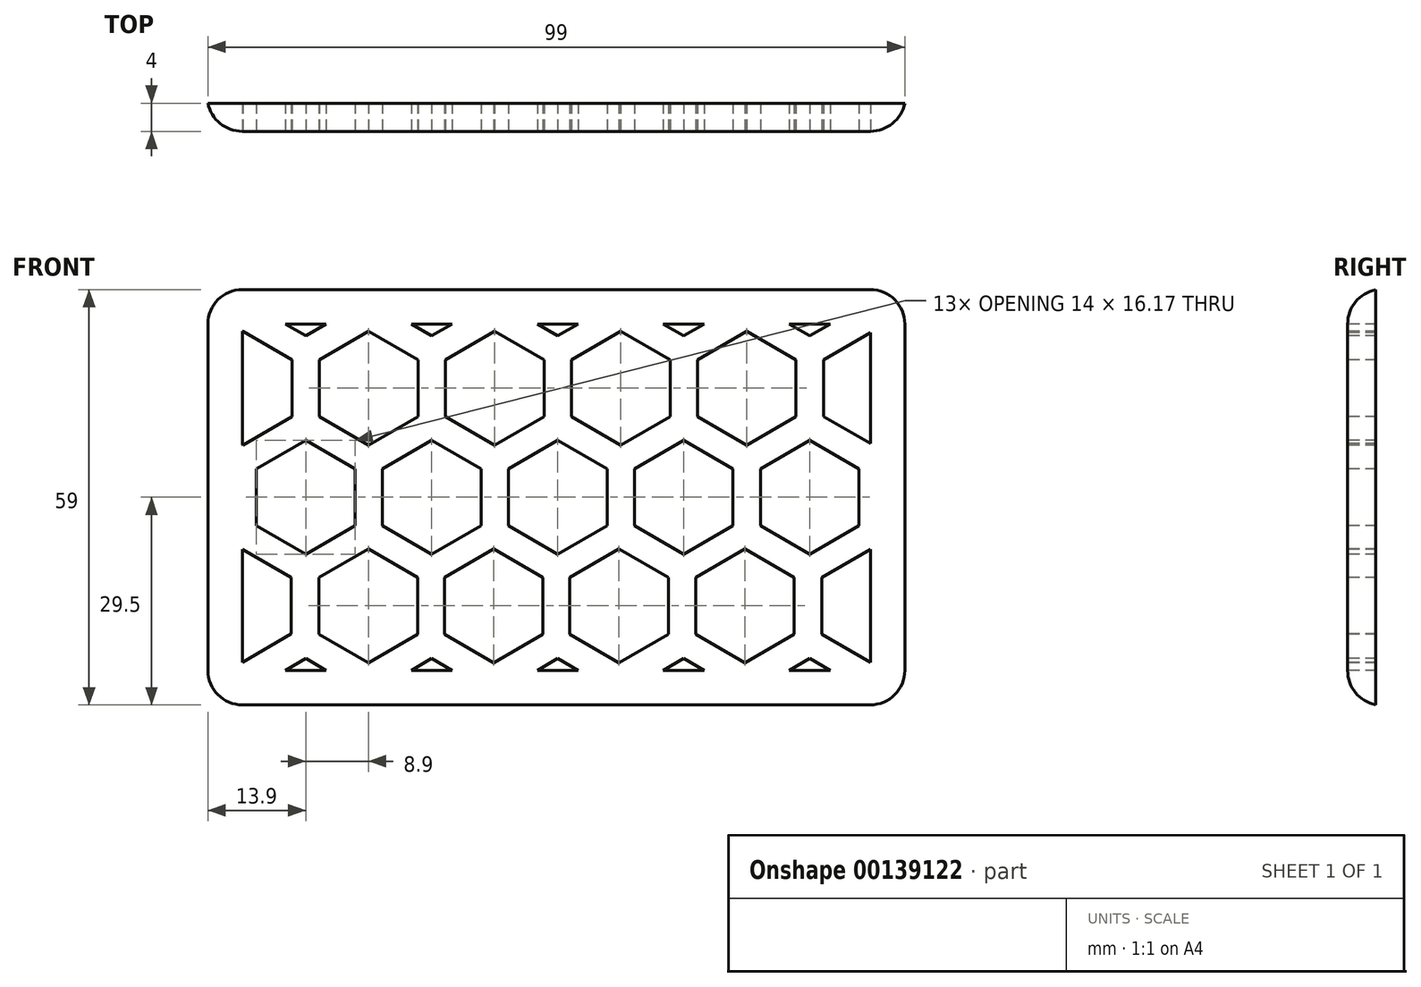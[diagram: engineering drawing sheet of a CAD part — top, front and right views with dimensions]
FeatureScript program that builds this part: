
annotation { "Feature Type Name" : "Feature", "Feature Type Description" : "" }
export const myFeature = defineFeature(function(context is Context, id is Id, definition is map)
    precondition{}
    {
        {
            var Q0;
            Q0=qCreatedBy(makeId("Front.planeOp"),FACE);
            var sketch = newSketch(context, id + "F0", { "sketchPlane" : qUnion([Q0])});
            skLineSegment(sketch, "E0.bottom", {"start": v(-49.5, -29.5) * mm, "end": v(49.5, -29.5) * mm});
            skLineSegment(sketch, "E0.top", {"start": v(-49.5, 29.5) * mm, "end": v(49.5, 29.5) * mm});
            skLineSegment(sketch, "E0.left", {"start": v(-49.5, -29.5) * mm, "end": v(-49.5, 29.5) * mm});
            skLineSegment(sketch, "E0.right", {"start": v(49.5, -29.5) * mm, "end": v(49.5, 29.5) * mm});
            skPoint(sketch, "E0.middle", {"position": v(0, 0) * mm});
            skSolve(sketch);
        }
        {
            var Q0;
            Q0=makeQuery(id+"F0.imprint","IMPRINT",FACE,{"disambiguationData":[TD([[makeQuery(id+"F0.imprint","IMPRINT",EDGE,{"derivedFrom":sQuery(id+"F0.wireOp",EDGE,"E0.bottom")}),1.0]])]});
            extrude(context, id + "F1", {"entities" : qUnion([Q0]), "depth" : 4 * mm});
        }
        {
            var Q0;
            Q0=makeQuery(id+"F1.opExtrude","CAP_EDGE",EDGE,{"disambiguationData":[OSD([sQuery(id+"F0.wireOp",EDGE,"E0.left")])],"isStart":false});
            var Q1;
            Q1=makeQuery(id+"F1.opExtrude","CAP_EDGE",EDGE,{"disambiguationData":[OSD([sQuery(id+"F0.wireOp",EDGE,"E0.top")])],"isStart":false});
            var Q2;
            Q2=makeQuery(id+"F1.opExtrude","CAP_EDGE",EDGE,{"disambiguationData":[OSD([sQuery(id+"F0.wireOp",EDGE,"E0.right")])],"isStart":false});
            var Q3;
            Q3=makeQuery(id+"F1.opExtrude","CAP_EDGE",EDGE,{"disambiguationData":[OSD([sQuery(id+"F0.wireOp",EDGE,"E0.bottom")])],"isStart":false});
            fillet(context, id + "F2", {"entities" : qUnion([Q0, Q1, Q2, Q3]), "radius" : 5 * mm, "tangentPropagation" : true, "allowEdgeOverflow" : false});
        }
        {
            var Q0;
            Q0=makeQuery(id+"F2.opFillet","BLEND_EDGE",EDGE,{"blendedFrom":[makeQuery(id+"F1.opExtrude","CAP_EDGE",EDGE,{"disambiguationData":[OSD([sQuery(id+"F0.wireOp",EDGE,"E0.top")])],"isStart":false}),makeQuery(id+"F1.opExtrude","CAP_EDGE",EDGE,{"disambiguationData":[OSD([sQuery(id+"F0.wireOp",EDGE,"E0.right")])],"isStart":false})],"blendedInto":[]});
            var Q1;
            Q1=makeQuery(id+"F2.opFillet","BLEND_EDGE",EDGE,{"blendedFrom":[makeQuery(id+"F1.opExtrude","CAP_EDGE",EDGE,{"disambiguationData":[OSD([sQuery(id+"F0.wireOp",EDGE,"E0.top")])],"isStart":false}),makeQuery(id+"F1.opExtrude","CAP_EDGE",EDGE,{"disambiguationData":[OSD([sQuery(id+"F0.wireOp",EDGE,"E0.left")])],"isStart":false})],"blendedInto":[]});
            var Q2;
            Q2=makeQuery(id+"F2.opFillet","BLEND_EDGE",EDGE,{"blendedFrom":[makeQuery(id+"F1.opExtrude","CAP_EDGE",EDGE,{"disambiguationData":[OSD([sQuery(id+"F0.wireOp",EDGE,"E0.bottom")])],"isStart":false}),makeQuery(id+"F1.opExtrude","CAP_EDGE",EDGE,{"disambiguationData":[OSD([sQuery(id+"F0.wireOp",EDGE,"E0.left")])],"isStart":false})],"blendedInto":[]});
            var Q3;
            Q3=makeQuery(id+"F2.opFillet","BLEND_EDGE",EDGE,{"blendedFrom":[makeQuery(id+"F1.opExtrude","CAP_EDGE",EDGE,{"disambiguationData":[OSD([sQuery(id+"F0.wireOp",EDGE,"E0.bottom")])],"isStart":false}),makeQuery(id+"F1.opExtrude","CAP_EDGE",EDGE,{"disambiguationData":[OSD([sQuery(id+"F0.wireOp",EDGE,"E0.right")])],"isStart":false})],"blendedInto":[]});
            fillet(context, id + "F3", {"entities" : qUnion([Q0, Q1, Q2, Q3]), "radius" : 5 * mm, "tangentPropagation" : true, "allowEdgeOverflow" : false});
        }
        {
            var Q0;
            Q0=makeQuery(id+"F1.opExtrude","CAP_FACE",FACE,{"disambiguationData":[OSD([sQuery(id+"F0.wireOp",EDGE,"E0.bottom"),sQuery(id+"F0.wireOp",EDGE,"E0.top"),sQuery(id+"F0.wireOp",EDGE,"E0.left"),sQuery(id+"F0.wireOp",EDGE,"E0.right")])],"isStart":false});
            var sketch = newSketch(context, id + "F4", { "sketchPlane" : qUnion([Q0])});
            skLineSegment(sketch, "E1", {"start": v(44.6, 0) * mm, "end": v(35.7, 0) * mm});
            skPoint(sketch, "E1.endSnap0", {"position": v(44.6, 0) * mm});
            skCircle(sketch, "E2.cCircle", {"center": v(35.7, 0) * mm, "radius": 8.9 * mm, "construction": true});
            skLineSegment(sketch, "E2.0", {"start": v(26.8, -5.14) * mm, "end": v(26.8, 5.14) * mm});
            skLineSegment(sketch, "E2.1", {"start": v(26.8, 5.14) * mm, "end": v(35.7, 10.28) * mm});
            skLineSegment(sketch, "E2.2", {"start": v(35.7, 10.28) * mm, "end": v(44.6, 5.14) * mm});
            skLineSegment(sketch, "E2.3", {"start": v(44.6, 5.14) * mm, "end": v(44.6, -5.14) * mm});
            skLineSegment(sketch, "E2.4", {"start": v(44.6, -5.14) * mm, "end": v(35.7, -10.28) * mm});
            skLineSegment(sketch, "E2.5", {"start": v(35.7, -10.28) * mm, "end": v(26.8, -5.14) * mm});
            skPoint(sketch, "E2.0.midPoint", {"position": v(26.8, 0) * mm});
            skLineSegment(sketch, "E3", {"start": v(26.8, 0) * mm, "end": v(17.9, 0) * mm});
            skCircle(sketch, "E4.cCircle", {"center": v(17.9, 0) * mm, "radius": 8.9 * mm, "construction": true});
            skLineSegment(sketch, "E4.0", {"start": v(9, -5.14) * mm, "end": v(9, 5.14) * mm});
            skLineSegment(sketch, "E4.1", {"start": v(9, 5.14) * mm, "end": v(17.9, 10.28) * mm});
            skLineSegment(sketch, "E4.2", {"start": v(17.9, 10.28) * mm, "end": v(26.8, 5.14) * mm});
            skLineSegment(sketch, "E4.3", {"start": v(26.8, 5.14) * mm, "end": v(26.8, -5.14) * mm});
            skLineSegment(sketch, "E4.4", {"start": v(26.8, -5.14) * mm, "end": v(17.9, -10.28) * mm});
            skLineSegment(sketch, "E4.5", {"start": v(17.9, -10.28) * mm, "end": v(9, -5.14) * mm});
            skPoint(sketch, "E4.0.midPoint", {"position": v(9, 0) * mm});
            skLineSegment(sketch, "E5", {"start": v(9, 0) * mm, "end": v(0.1, 0) * mm});
            skCircle(sketch, "E6.cCircle", {"center": v(0, 0) * mm, "radius": 8.9 * mm, "construction": true});
            skLineSegment(sketch, "E6.0", {"start": v(-8.9, -5.14) * mm, "end": v(-8.9, 5.14) * mm});
            skLineSegment(sketch, "E6.1", {"start": v(-8.9, 5.14) * mm, "end": v(0, 10.28) * mm});
            skLineSegment(sketch, "E6.2", {"start": v(0, 10.28) * mm, "end": v(8.9, 5.14) * mm});
            skLineSegment(sketch, "E6.3", {"start": v(8.9, 5.14) * mm, "end": v(8.9, -5.14) * mm});
            skLineSegment(sketch, "E6.4", {"start": v(8.9, -5.14) * mm, "end": v(0, -10.28) * mm});
            skLineSegment(sketch, "E6.5", {"start": v(0, -10.28) * mm, "end": v(-8.9, -5.14) * mm});
            skPoint(sketch, "E6.0.midPoint", {"position": v(-8.9, 0) * mm});
            skLineSegment(sketch, "E7", {"start": v(-8.9, 0) * mm, "end": v(-17.8, 0) * mm});
            skCircle(sketch, "E8.cCircle", {"center": v(-17.8, 0) * mm, "radius": 8.9 * mm, "construction": true});
            skLineSegment(sketch, "E8.0", {"start": v(-26.7, -5.14) * mm, "end": v(-26.7, 5.14) * mm});
            skLineSegment(sketch, "E8.1", {"start": v(-26.7, 5.14) * mm, "end": v(-17.8, 10.28) * mm});
            skLineSegment(sketch, "E8.2", {"start": v(-17.8, 10.28) * mm, "end": v(-8.9, 5.14) * mm});
            skLineSegment(sketch, "E8.3", {"start": v(-8.9, 5.14) * mm, "end": v(-8.9, -5.14) * mm});
            skLineSegment(sketch, "E8.4", {"start": v(-8.9, -5.14) * mm, "end": v(-17.8, -10.28) * mm});
            skLineSegment(sketch, "E8.5", {"start": v(-17.8, -10.28) * mm, "end": v(-26.7, -5.14) * mm});
            skPoint(sketch, "E8.0.midPoint", {"position": v(-26.7, 0) * mm});
            skLineSegment(sketch, "E9", {"start": v(-26.7, 0) * mm, "end": v(-35.6, 0) * mm});
            skCircle(sketch, "E10.cCircle", {"center": v(-35.6, 0) * mm, "radius": 9 * mm, "construction": true});
            skLineSegment(sketch, "E10.0", {"start": v(-44.6, -5.2) * mm, "end": v(-44.6, 5.2) * mm});
            skLineSegment(sketch, "E10.1", {"start": v(-44.6, 5.2) * mm, "end": v(-35.6, 10.4) * mm});
            skLineSegment(sketch, "E10.2", {"start": v(-35.6, 10.4) * mm, "end": v(-26.6, 5.2) * mm});
            skLineSegment(sketch, "E10.3", {"start": v(-26.6, 5.2) * mm, "end": v(-26.6, -5.2) * mm});
            skLineSegment(sketch, "E10.4", {"start": v(-26.6, -5.2) * mm, "end": v(-35.6, -10.4) * mm});
            skLineSegment(sketch, "E10.5", {"start": v(-35.6, -10.4) * mm, "end": v(-44.6, -5.2) * mm});
            skPoint(sketch, "E10.0.midPoint", {"position": v(-44.6, 0) * mm});
            skLineSegment(sketch, "E11", {"start": v(-31.1, 7.8) * mm, "end": v(-26.65, 15.5) * mm});
            skCircle(sketch, "E12.cCircle", {"center": v(-26.65, 15.5) * mm, "radius": 8.9 * mm, "construction": true});
            skLineSegment(sketch, "E12.0", {"start": v(-35.55, 10.36) * mm, "end": v(-35.55, 20.64) * mm});
            skLineSegment(sketch, "E12.1", {"start": v(-35.55, 20.64) * mm, "end": v(-28.7, 24.6) * mm});
            skLineSegment(sketch, "E12.2", {"start": v(-24.6, 24.6) * mm, "end": v(-17.75, 20.64) * mm});
            skLineSegment(sketch, "E12.3", {"start": v(-17.75, 20.64) * mm, "end": v(-17.75, 10.36) * mm});
            skLineSegment(sketch, "E12.4", {"start": v(-17.75, 10.36) * mm, "end": v(-26.65, 5.23) * mm});
            skLineSegment(sketch, "E12.5", {"start": v(-26.65, 5.23) * mm, "end": v(-35.55, 10.36) * mm});
            skPoint(sketch, "E12.0.midPoint", {"position": v(-35.55, 15.5) * mm});
            skLineSegment(sketch, "E13", {"start": v(-44.6, 24.6) * mm, "end": v(44.6, 24.6) * mm});
            skLineSegment(sketch, "E14", {"start": v(-44.6, 24.6) * mm, "end": v(-44.6, -24.6) * mm});
            skLineSegment(sketch, "E15", {"start": v(-44.6, -24.6) * mm, "end": v(44.6, -24.6) * mm});
            skLineSegment(sketch, "E16", {"start": v(44.6, -24.6) * mm, "end": v(44.6, 24.6) * mm});
            skPoint(sketch, "E17.orphan", {"position": v(-26.65, 25.78) * mm});
            skLineSegment(sketch, "E18", {"start": v(-40.1, 7.8) * mm, "end": v(-44.55, 15.5) * mm});
            skArc(sketch, "E19.cCircle", {"start": v(-44.6, 6.6) * mm, "mid": v(-35.65, 15.5) * mm, "end": v(-44.6, 24.4) * mm, "construction": true});
            skLineSegment(sketch, "E19.2", {"start": v(-44.55, 25.78) * mm, "end": v(-35.65, 20.64) * mm});
            skLineSegment(sketch, "E19.3", {"start": v(-35.65, 20.64) * mm, "end": v(-35.65, 10.36) * mm});
            skLineSegment(sketch, "E19.4", {"start": v(-35.65, 10.36) * mm, "end": v(-44.55, 5.23) * mm});
            skLineSegment(sketch, "E19.5", {"start": v(-44.55, 5.23) * mm, "end": v(-44.6, 5.26) * mm});
            skPoint(sketch, "E19.0.midPoint", {"position": v(-53.45, 15.5) * mm});
            skPoint(sketch, "E20.orphan", {"position": v(-53.45, 20.64) * mm});
            skPoint(sketch, "E21.orphan", {"position": v(-53.45, 10.36) * mm});
            skCircle(sketch, "E22.cCircle", {"center": v(-8.9, 15.42) * mm, "radius": 8.9 * mm, "construction": true});
            skLineSegment(sketch, "E22.0", {"start": v(-17.42, 9.66) * mm, "end": v(-18.14, 19.92) * mm});
            skLineSegment(sketch, "E22.1", {"start": v(-18.14, 19.92) * mm, "end": v(-11.2, 24.6) * mm});
            skLineSegment(sketch, "E22.2", {"start": v(-7.43, 24.6) * mm, "end": v(-0.38, 21.17) * mm});
            skLineSegment(sketch, "E22.3", {"start": v(-0.38, 21.17) * mm, "end": v(0.34, 10.91) * mm});
            skLineSegment(sketch, "E22.4", {"start": v(0.34, 10.91) * mm, "end": v(-8.18, 5.16) * mm});
            skLineSegment(sketch, "E22.5", {"start": v(-8.18, 5.16) * mm, "end": v(-17.42, 9.66) * mm});
            skPoint(sketch, "E22.0.midPoint", {"position": v(-17.78, 14.8) * mm});
            skPoint(sketch, "E23.orphan", {"position": v(-9.62, 25.67) * mm});
            skLineSegment(sketch, "E24", {"start": v(-22.25, -7.7) * mm, "end": v(-26.7, -15.42) * mm});
            skCircle(sketch, "E25.cCircle", {"center": v(-26.7, -15.42) * mm, "radius": 8.9 * mm, "construction": true});
            skLineSegment(sketch, "E25.0", {"start": v(-35.6, -20.55) * mm, "end": v(-35.6, -10.28) * mm});
            skLineSegment(sketch, "E25.1", {"start": v(-35.6, -10.28) * mm, "end": v(-26.7, -5.14) * mm});
            skLineSegment(sketch, "E25.2", {"start": v(-26.7, -5.14) * mm, "end": v(-17.8, -10.28) * mm});
            skLineSegment(sketch, "E25.3", {"start": v(-17.8, -10.28) * mm, "end": v(-17.8, -20.55) * mm});
            skLineSegment(sketch, "E25.4", {"start": v(-17.8, -20.55) * mm, "end": v(-24.81, -24.6) * mm});
            skLineSegment(sketch, "E25.5", {"start": v(-28.59, -24.6) * mm, "end": v(-35.6, -20.55) * mm});
            skPoint(sketch, "E25.0.midPoint", {"position": v(-35.6, -15.42) * mm});
            skLineSegment(sketch, "E26", {"start": v(-4.45, -7.7) * mm, "end": v(-8.9, -15.42) * mm});
            skPoint(sketch, "E26.endSnap0", {"position": v(-17.8, -15.42) * mm});
            skCircle(sketch, "E27.cCircle", {"center": v(-8.9, -15.42) * mm, "radius": 8.9 * mm, "construction": true});
            skLineSegment(sketch, "E27.0", {"start": v(-17.8, -20.55) * mm, "end": v(-17.8, -10.28) * mm});
            skLineSegment(sketch, "E27.1", {"start": v(-17.8, -10.28) * mm, "end": v(-8.9, -5.14) * mm});
            skLineSegment(sketch, "E27.2", {"start": v(-8.9, -5.14) * mm, "end": v(0, -10.28) * mm});
            skLineSegment(sketch, "E27.3", {"start": v(0, -10.28) * mm, "end": v(0, -20.55) * mm});
            skLineSegment(sketch, "E27.4", {"start": v(0, -20.55) * mm, "end": v(-7.01, -24.6) * mm});
            skLineSegment(sketch, "E27.5", {"start": v(-10.79, -24.6) * mm, "end": v(-17.8, -20.55) * mm});
            skLineSegment(sketch, "E28", {"start": v(4.45, -7.7) * mm, "end": v(8.9, -15.42) * mm});
            skCircle(sketch, "E29.cCircle", {"center": v(8.9, -15.42) * mm, "radius": 8.85 * mm, "construction": true});
            skPoint(sketch, "E29.cCircle.perimeterSnap0", {"position": v(0, -15.42) * mm});
            skLineSegment(sketch, "E29.0", {"start": v(0.05, -20.52) * mm, "end": v(0.05, -10.3) * mm});
            skLineSegment(sketch, "E29.1", {"start": v(0.05, -10.3) * mm, "end": v(8.9, -5.2) * mm});
            skLineSegment(sketch, "E29.2", {"start": v(8.9, -5.2) * mm, "end": v(17.75, -10.3) * mm});
            skLineSegment(sketch, "E29.3", {"start": v(17.75, -10.3) * mm, "end": v(17.75, -20.52) * mm});
            skLineSegment(sketch, "E29.4", {"start": v(17.75, -20.52) * mm, "end": v(10.69, -24.6) * mm});
            skLineSegment(sketch, "E29.5", {"start": v(7.11, -24.6) * mm, "end": v(0.05, -20.52) * mm});
            skPoint(sketch, "E29.0.midPoint", {"position": v(0.05, -15.42) * mm});
            skPoint(sketch, "E29.0.midPoint.positionSnap0", {"position": v(0, -15.42) * mm});
            skLineSegment(sketch, "E30", {"start": v(13.45, 7.7) * mm, "end": v(9, 15.42) * mm});
            skCircle(sketch, "E31.cCircle", {"center": v(9, 15.42) * mm, "radius": 8.9 * mm, "construction": true});
            skLineSegment(sketch, "E31.0", {"start": v(0.1, 10.28) * mm, "end": v(0.1, 20.55) * mm});
            skLineSegment(sketch, "E31.1", {"start": v(0.1, 20.55) * mm, "end": v(9, 25.7) * mm});
            skLineSegment(sketch, "E31.2", {"start": v(9, 25.7) * mm, "end": v(17.9, 20.55) * mm});
            skLineSegment(sketch, "E31.3", {"start": v(17.9, 20.55) * mm, "end": v(17.9, 10.28) * mm});
            skLineSegment(sketch, "E31.4", {"start": v(17.9, 10.28) * mm, "end": v(9, 5.14) * mm});
            skLineSegment(sketch, "E31.5", {"start": v(9, 5.14) * mm, "end": v(0.1, 10.28) * mm});
            skPoint(sketch, "E31.0.midPoint", {"position": v(0.1, 15.42) * mm});
            skLineSegment(sketch, "E32", {"start": v(22.35, 7.7) * mm, "end": v(26.8, 15.42) * mm});
            skCircle(sketch, "E33.cCircle", {"center": v(26.8, 15.42) * mm, "radius": 8.9 * mm, "construction": true});
            skLineSegment(sketch, "E33.0", {"start": v(17.9, 10.28) * mm, "end": v(17.9, 20.55) * mm});
            skLineSegment(sketch, "E33.1", {"start": v(17.9, 20.55) * mm, "end": v(24.91, 24.6) * mm});
            skLineSegment(sketch, "E33.2", {"start": v(26.8, 25.7) * mm, "end": v(26.83, 25.68) * mm});
            skLineSegment(sketch, "E33.3", {"start": v(35.7, 20.55) * mm, "end": v(35.7, 10.28) * mm});
            skLineSegment(sketch, "E33.4", {"start": v(35.7, 10.28) * mm, "end": v(26.8, 5.14) * mm});
            skLineSegment(sketch, "E33.5", {"start": v(26.8, 5.14) * mm, "end": v(17.9, 10.28) * mm});
            skPoint(sketch, "E33.0.midPoint", {"position": v(17.9, 15.42) * mm});
            skLineSegment(sketch, "E34", {"start": v(22.35, -7.7) * mm, "end": v(26.8, -15.42) * mm});
            skCircle(sketch, "E35.cCircle", {"center": v(26.8, -15.42) * mm, "radius": 8.9 * mm, "construction": true});
            skLineSegment(sketch, "E35.0", {"start": v(17.9, -20.55) * mm, "end": v(17.9, -10.28) * mm});
            skLineSegment(sketch, "E35.1", {"start": v(17.9, -10.28) * mm, "end": v(26.8, -5.14) * mm});
            skLineSegment(sketch, "E35.2", {"start": v(26.8, -5.14) * mm, "end": v(35.7, -10.28) * mm});
            skLineSegment(sketch, "E35.3", {"start": v(35.7, -10.28) * mm, "end": v(35.7, -20.55) * mm});
            skLineSegment(sketch, "E35.4", {"start": v(35.7, -20.55) * mm, "end": v(28.7, -24.6) * mm});
            skLineSegment(sketch, "E35.5", {"start": v(24.91, -24.6) * mm, "end": v(17.9, -20.55) * mm});
            skPoint(sketch, "E35.0.midPoint", {"position": v(17.9, -15.42) * mm});
            skLineSegment(sketch, "E36", {"start": v(35.7, -15.42) * mm, "end": v(44.6, -15.42) * mm});
            skArc(sketch, "E37.cCircle", {"start": v(44.6, -6.52) * mm, "mid": v(35.7, -15.42) * mm, "end": v(44.6, -24.32) * mm, "construction": true});
            skLineSegment(sketch, "E37.0", {"start": v(35.7, -20.55) * mm, "end": v(35.7, -10.28) * mm});
            skLineSegment(sketch, "E37.1", {"start": v(35.7, -10.28) * mm, "end": v(44.6, -5.14) * mm});
            skLineSegment(sketch, "E37.5", {"start": v(44.6, -25.7) * mm, "end": v(35.7, -20.55) * mm});
            skPoint(sketch, "E37.0.midPoint", {"position": v(35.7, -15.42) * mm});
            skLineSegment(sketch, "E38", {"start": v(35.7, 15.42) * mm, "end": v(44.6, 15.42) * mm});
            skArc(sketch, "E39.cCircle", {"start": v(44.6, 24.27) * mm, "mid": v(35.75, 15.42) * mm, "end": v(44.6, 6.57) * mm, "construction": true});
            skLineSegment(sketch, "E39.0", {"start": v(35.75, 10.3) * mm, "end": v(35.75, 20.52) * mm});
            skLineSegment(sketch, "E39.1", {"start": v(35.75, 20.52) * mm, "end": v(42.81, 24.6) * mm});
            skLineSegment(sketch, "E39.5", {"start": v(44.6, 5.2) * mm, "end": v(35.75, 10.3) * mm});
            skPoint(sketch, "E39.0.midPoint", {"position": v(35.75, 15.42) * mm});
            skLineSegment(sketch, "E40", {"start": v(40.18, 23.08) * mm, "end": v(35.73, 30.79) * mm});
            skArc(sketch, "E41.cCircle", {"start": v(29.33, 24.6) * mm, "mid": v(35.73, 21.89) * mm, "end": v(42.12, 24.6) * mm, "construction": true});
            skLineSegment(sketch, "E41.0", {"start": v(26.83, 25.65) * mm, "end": v(26.83, 25.68) * mm});
            skLineSegment(sketch, "E41.4", {"start": v(44.63, 25.65) * mm, "end": v(35.73, 20.51) * mm});
            skLineSegment(sketch, "E41.5", {"start": v(35.73, 20.51) * mm, "end": v(28.64, 24.6) * mm});
            skPoint(sketch, "E41.0.midPoint", {"position": v(26.83, 30.79) * mm});
            skLineSegment(sketch, "E42", {"start": v(22.35, 23.12) * mm, "end": v(17.9, 30.83) * mm});
            skArc(sketch, "E43.cCircle", {"start": v(11.54, 24.6) * mm, "mid": v(17.9, 21.93) * mm, "end": v(24.26, 24.6) * mm, "construction": true});
            skLineSegment(sketch, "E43.0", {"start": v(9, 25.7) * mm, "end": v(9, 35.97) * mm});
            skLineSegment(sketch, "E43.4", {"start": v(24.91, 24.6) * mm, "end": v(17.9, 20.55) * mm});
            skLineSegment(sketch, "E43.5", {"start": v(17.9, 20.55) * mm, "end": v(10.9, 24.6) * mm});
            skPoint(sketch, "E43.0.midPoint", {"position": v(9, 30.83) * mm});
            skLineSegment(sketch, "E44", {"start": v(9, 30.83) * mm, "end": v(0.1, 30.83) * mm});
            skArc(sketch, "E45.cCircle", {"start": v(-6.26, 24.6) * mm, "mid": v(8.34, 34.2) * mm, "end": v(-8.8, 30.83) * mm, "construction": true});
            skLineSegment(sketch, "E45.1", {"start": v(-8.8, 35.97) * mm, "end": v(0.1, 41.1) * mm});
            skLineSegment(sketch, "E45.2", {"start": v(0.1, 41.1) * mm, "end": v(9, 35.97) * mm});
            skLineSegment(sketch, "E45.3", {"start": v(9, 30.83) * mm, "end": v(9, 25.7) * mm});
            skLineSegment(sketch, "E45.4", {"start": v(9, 25.7) * mm, "end": v(0.1, 20.55) * mm});
            skLineSegment(sketch, "E45.5", {"start": v(0.1, 20.55) * mm, "end": v(-6.9, 24.6) * mm});
            skPoint(sketch, "E45.0.midPoint", {"position": v(-8.8, 30.83) * mm});
            skPoint(sketch, "E46.orphan", {"position": v(-26.7, -25.7) * mm});
            skPoint(sketch, "E47.orphan", {"position": v(-8.9, -25.7) * mm});
            skPoint(sketch, "E48.orphan", {"position": v(8.9, -25.63) * mm});
            skLineSegment(sketch, "E49.0.1", {"start": v(-44.6, -24.6) * mm, "end": v(-44.6, -29.5) * mm});
            skLineSegment(sketch, "E49.0.2", {"start": v(-44.6, -29.5) * mm, "end": v(44.6, -29.5) * mm});
            skLineSegment(sketch, "E49.0.3", {"start": v(44.6, -29.5) * mm, "end": v(44.6, -24.6) * mm});
            skPoint(sketch, "E50.orphan", {"position": v(44.6, 25.63) * mm});
            skLineSegment(sketch, "E51.trimOffspring", {"start": v(28.7, 24.6) * mm, "end": v(35.7, 20.55) * mm});
            skPoint(sketch, "E52.trimOffspring.end.orphan", {"position": v(26.83, 35.93) * mm});
            skPoint(sketch, "E53.orphan", {"position": v(-8.8, 25.7) * mm});
            skCircle(sketch, "E54.cCircle", {"center": v(-35.6, 0) * mm, "radius": 7 * mm, "construction": true});
            skLineSegment(sketch, "E54.0", {"start": v(-42.6, -4.04) * mm, "end": v(-42.6, 4.04) * mm});
            skLineSegment(sketch, "E54.1", {"start": v(-42.6, 4.04) * mm, "end": v(-35.6, 8.08) * mm});
            skLineSegment(sketch, "E54.2", {"start": v(-35.6, 8.08) * mm, "end": v(-28.6, 4.04) * mm});
            skLineSegment(sketch, "E54.3", {"start": v(-28.6, 4.04) * mm, "end": v(-28.6, -4.04) * mm});
            skLineSegment(sketch, "E54.4", {"start": v(-28.6, -4.04) * mm, "end": v(-35.6, -8.08) * mm});
            skLineSegment(sketch, "E54.5", {"start": v(-35.6, -8.08) * mm, "end": v(-42.6, -4.04) * mm});
            skPoint(sketch, "E54.0.midPoint", {"position": v(-42.6, 0) * mm});
            skCircle(sketch, "E55.cCircle", {"center": v(-26.65, 15.5) * mm, "radius": 7 * mm, "construction": true});
            skLineSegment(sketch, "E55.0", {"start": v(-33.65, 11.46) * mm, "end": v(-33.65, 19.54) * mm});
            skLineSegment(sketch, "E55.1", {"start": v(-33.65, 19.54) * mm, "end": v(-26.65, 23.59) * mm});
            skLineSegment(sketch, "E55.2", {"start": v(-26.65, 23.59) * mm, "end": v(-19.65, 19.54) * mm});
            skLineSegment(sketch, "E55.3", {"start": v(-19.65, 19.54) * mm, "end": v(-19.65, 11.46) * mm});
            skLineSegment(sketch, "E55.4", {"start": v(-19.65, 11.46) * mm, "end": v(-26.65, 7.42) * mm});
            skLineSegment(sketch, "E55.5", {"start": v(-26.65, 7.42) * mm, "end": v(-33.65, 11.46) * mm});
            skPoint(sketch, "E55.0.midPoint", {"position": v(-33.65, 15.5) * mm});
            skCircle(sketch, "E56.cCircle", {"center": v(-26.7, -15.42) * mm, "radius": 7 * mm, "construction": true});
            skLineSegment(sketch, "E56.0", {"start": v(-33.7, -19.46) * mm, "end": v(-33.7, -11.37) * mm});
            skLineSegment(sketch, "E56.1", {"start": v(-33.7, -11.37) * mm, "end": v(-26.7, -7.33) * mm});
            skLineSegment(sketch, "E56.2", {"start": v(-26.7, -7.33) * mm, "end": v(-19.7, -11.37) * mm});
            skLineSegment(sketch, "E56.3", {"start": v(-19.7, -11.37) * mm, "end": v(-19.7, -19.46) * mm});
            skLineSegment(sketch, "E56.4", {"start": v(-19.7, -19.46) * mm, "end": v(-26.7, -23.5) * mm});
            skLineSegment(sketch, "E56.5", {"start": v(-26.7, -23.5) * mm, "end": v(-33.7, -19.46) * mm});
            skPoint(sketch, "E56.0.midPoint", {"position": v(-33.7, -15.42) * mm});
            skCircle(sketch, "E57.cCircle", {"center": v(-8.9, -15.42) * mm, "radius": 7 * mm, "construction": true});
            skLineSegment(sketch, "E57.0", {"start": v(-15.9, -19.46) * mm, "end": v(-15.9, -11.37) * mm});
            skLineSegment(sketch, "E57.1", {"start": v(-15.9, -11.37) * mm, "end": v(-8.9, -7.33) * mm});
            skLineSegment(sketch, "E57.2", {"start": v(-8.9, -7.33) * mm, "end": v(-1.9, -11.37) * mm});
            skLineSegment(sketch, "E57.3", {"start": v(-1.9, -11.37) * mm, "end": v(-1.9, -19.46) * mm});
            skLineSegment(sketch, "E57.4", {"start": v(-1.9, -19.46) * mm, "end": v(-8.9, -23.5) * mm});
            skLineSegment(sketch, "E57.5", {"start": v(-8.9, -23.5) * mm, "end": v(-15.9, -19.46) * mm});
            skPoint(sketch, "E57.0.midPoint", {"position": v(-15.9, -15.42) * mm});
            skPoint(sketch, "E58.cCircle.perimeterSnap0", {"position": v(4.55, 7.7) * mm});
            skPoint(sketch, "E58.0.midPoint.positionSnap0", {"position": v(4.55, 7.7) * mm});
            skCircle(sketch, "E59.cCircle", {"center": v(8.9, -15.42) * mm, "radius": 7 * mm, "construction": true});
            skLineSegment(sketch, "E59.0", {"start": v(1.9, -19.46) * mm, "end": v(1.9, -11.37) * mm});
            skLineSegment(sketch, "E59.1", {"start": v(1.9, -11.37) * mm, "end": v(8.9, -7.33) * mm});
            skLineSegment(sketch, "E59.2", {"start": v(8.9, -7.33) * mm, "end": v(15.9, -11.37) * mm});
            skLineSegment(sketch, "E59.3", {"start": v(15.9, -11.37) * mm, "end": v(15.9, -19.46) * mm});
            skLineSegment(sketch, "E59.4", {"start": v(15.9, -19.46) * mm, "end": v(8.9, -23.5) * mm});
            skLineSegment(sketch, "E59.5", {"start": v(8.9, -23.5) * mm, "end": v(1.9, -19.46) * mm});
            skPoint(sketch, "E59.0.midPoint", {"position": v(1.9, -15.42) * mm});
            skSolve(sketch);
        }
        {
            var Q0;
            {var subQ3=sQuery(id+"F4.wireOp",EDGE,"E59.0");Q0=makeQuery(id+"F4.imprint","IMPRINT",FACE,{"disambiguationData":[TD([[makeQuery(id+"F4.imprint","IMPRINT",EDGE,{"derivedFrom":subQ3}),-1.0]])]});}
            var Q1;
            Q1=makeQuery(id+"F4.imprint","IMPRINT",FACE,{"disambiguationData":[TD([[makeQuery(id+"F4.imprint","IMPRINT",EDGE,{"derivedFrom":sQuery(id+"F4.wireOp",EDGE,"E57.0")}),-1.0]])]});
            var Q2;
            Q2=makeQuery(id+"F4.imprint","IMPRINT",FACE,{"disambiguationData":[TD([[makeQuery(id+"F4.imprint","IMPRINT",EDGE,{"derivedFrom":sQuery(id+"F4.wireOp",EDGE,"E56.0")}),-1.0]])]});
            var Q3;
            Q3=makeQuery(id+"F4.imprint","IMPRINT",FACE,{"disambiguationData":[TD([[makeQuery(id+"F4.imprint","IMPRINT",EDGE,{"derivedFrom":sQuery(id+"F4.wireOp",EDGE,"E54.0")}),-1.0]])]});
            var Q4;
            {var subQ0=sQuery(id+"F4.wireOp",EDGE,"E55.0");Q4=makeQuery(id+"F4.imprint","IMPRINT",FACE,{"disambiguationData":[TD([[makeQuery(id+"F4.imprint","IMPRINT",EDGE,{"derivedFrom":subQ0}),-1.0]])]});}
            extrude(context, id + "F5", {"entities" : qUnion([Q0, Q1, Q2, Q3, Q4]), "operationType" : NewBodyOperationType.REMOVE, "oppositeDirection" : true, "depth" : 25 * mm});
        }
        {
            var Q0;
            Q0=makeQuery(id+"F1.opExtrude","CAP_FACE",FACE,{"disambiguationData":[OSD([sQuery(id+"F0.wireOp",EDGE,"E0.bottom"),sQuery(id+"F0.wireOp",EDGE,"E0.top"),sQuery(id+"F0.wireOp",EDGE,"E0.left"),sQuery(id+"F0.wireOp",EDGE,"E0.right")])],"isStart":false});
            var sketch = newSketch(context, id + "F6", { "sketchPlane" : qUnion([Q0])});
            skLineSegment(sketch, "E60", {"start": v(-26.65, 23.59) * mm, "end": v(-26.65, 7.42) * mm});
            skLineSegment(sketch, "E61", {"start": v(-26.65, 15.5) * mm, "end": v(-35.6, 0) * mm});
            skLineSegment(sketch, "E62", {"start": v(-35.6, 0) * mm, "end": v(-17.7, 0) * mm});
            skCircle(sketch, "E63.cCircle", {"center": v(-17.7, 0) * mm, "radius": 7 * mm, "construction": true});
            skLineSegment(sketch, "E63.0", {"start": v(-24.7, -4.04) * mm, "end": v(-24.7, 4.04) * mm});
            skLineSegment(sketch, "E63.1", {"start": v(-24.7, 4.04) * mm, "end": v(-17.7, 8.08) * mm});
            skLineSegment(sketch, "E63.2", {"start": v(-17.7, 8.08) * mm, "end": v(-10.7, 4.04) * mm});
            skLineSegment(sketch, "E63.3", {"start": v(-10.7, 4.04) * mm, "end": v(-10.7, -4.04) * mm});
            skLineSegment(sketch, "E63.4", {"start": v(-10.7, -4.04) * mm, "end": v(-17.7, -8.08) * mm});
            skLineSegment(sketch, "E63.5", {"start": v(-17.7, -8.08) * mm, "end": v(-24.7, -4.04) * mm});
            skPoint(sketch, "E63.0.midPoint", {"position": v(-24.7, 0) * mm});
            skLineSegment(sketch, "E64", {"start": v(-26.65, 15.5) * mm, "end": v(-8.75, 15.5) * mm});
            skCircle(sketch, "E65.cCircle", {"center": v(-8.75, 15.5) * mm, "radius": 7 * mm, "construction": true});
            skLineSegment(sketch, "E65.0", {"start": v(-15.75, 11.46) * mm, "end": v(-15.75, 19.54) * mm});
            skLineSegment(sketch, "E65.1", {"start": v(-15.75, 19.54) * mm, "end": v(-8.75, 23.59) * mm});
            skLineSegment(sketch, "E65.2", {"start": v(-8.75, 23.59) * mm, "end": v(-1.75, 19.54) * mm});
            skLineSegment(sketch, "E65.3", {"start": v(-1.75, 19.54) * mm, "end": v(-1.75, 11.46) * mm});
            skLineSegment(sketch, "E65.4", {"start": v(-1.75, 11.46) * mm, "end": v(-8.75, 7.42) * mm});
            skLineSegment(sketch, "E65.5", {"start": v(-8.75, 7.42) * mm, "end": v(-15.75, 11.46) * mm});
            skPoint(sketch, "E65.0.midPoint", {"position": v(-15.75, 15.5) * mm});
            skLineSegment(sketch, "E66", {"start": v(-17.7, 0) * mm, "end": v(0.2, 0) * mm});
            skCircle(sketch, "E67.cCircle", {"center": v(0.2, 0) * mm, "radius": 7 * mm, "construction": true});
            skLineSegment(sketch, "E67.0", {"start": v(-6.8, -4.04) * mm, "end": v(-6.8, 4.04) * mm});
            skLineSegment(sketch, "E67.1", {"start": v(-6.8, 4.04) * mm, "end": v(0.2, 8.08) * mm});
            skLineSegment(sketch, "E67.2", {"start": v(0.2, 8.08) * mm, "end": v(7.2, 4.04) * mm});
            skLineSegment(sketch, "E67.3", {"start": v(7.2, 4.04) * mm, "end": v(7.2, -4.04) * mm});
            skLineSegment(sketch, "E67.4", {"start": v(7.2, -4.04) * mm, "end": v(0.2, -8.08) * mm});
            skLineSegment(sketch, "E67.5", {"start": v(0.2, -8.08) * mm, "end": v(-6.8, -4.04) * mm});
            skPoint(sketch, "E67.0.midPoint", {"position": v(-6.8, 0) * mm});
            skLineSegment(sketch, "E68", {"start": v(-8.75, 15.5) * mm, "end": v(9.15, 15.5) * mm});
            skCircle(sketch, "E69.cCircle", {"center": v(9.15, 15.5) * mm, "radius": 7 * mm, "construction": true});
            skLineSegment(sketch, "E69.0", {"start": v(2.15, 11.46) * mm, "end": v(2.15, 19.54) * mm});
            skLineSegment(sketch, "E69.1", {"start": v(2.15, 19.54) * mm, "end": v(9.15, 23.59) * mm});
            skLineSegment(sketch, "E69.2", {"start": v(9.15, 23.59) * mm, "end": v(16.15, 19.54) * mm});
            skLineSegment(sketch, "E69.3", {"start": v(16.15, 19.54) * mm, "end": v(16.15, 11.46) * mm});
            skLineSegment(sketch, "E69.4", {"start": v(16.15, 11.46) * mm, "end": v(9.15, 7.42) * mm});
            skLineSegment(sketch, "E69.5", {"start": v(9.15, 7.42) * mm, "end": v(2.15, 11.46) * mm});
            skPoint(sketch, "E69.0.midPoint", {"position": v(2.15, 15.5) * mm});
            skLineSegment(sketch, "E70", {"start": v(9.15, 15.5) * mm, "end": v(27.05, 15.5) * mm});
            skCircle(sketch, "E71.cCircle", {"center": v(27.05, 15.5) * mm, "radius": 7 * mm, "construction": true});
            skLineSegment(sketch, "E71.0", {"start": v(20.05, 11.46) * mm, "end": v(20.05, 19.54) * mm});
            skLineSegment(sketch, "E71.1", {"start": v(20.05, 19.54) * mm, "end": v(27.05, 23.59) * mm});
            skLineSegment(sketch, "E71.2", {"start": v(27.05, 23.59) * mm, "end": v(34.05, 19.54) * mm});
            skLineSegment(sketch, "E71.3", {"start": v(34.05, 19.54) * mm, "end": v(34.05, 11.46) * mm});
            skLineSegment(sketch, "E71.4", {"start": v(34.05, 11.46) * mm, "end": v(27.05, 7.42) * mm});
            skLineSegment(sketch, "E71.5", {"start": v(27.05, 7.42) * mm, "end": v(20.05, 11.46) * mm});
            skPoint(sketch, "E71.0.midPoint", {"position": v(20.05, 15.5) * mm});
            skLineSegment(sketch, "E72", {"start": v(8.9, -7.33) * mm, "end": v(8.9, -23.5) * mm});
            skLineSegment(sketch, "E73", {"start": v(8.9, -15.42) * mm, "end": v(26.8, -15.42) * mm});
            skCircle(sketch, "E74.cCircle", {"center": v(26.8, -15.42) * mm, "radius": 7 * mm, "construction": true});
            skLineSegment(sketch, "E74.0", {"start": v(19.8, -19.46) * mm, "end": v(19.8, -11.37) * mm});
            skLineSegment(sketch, "E74.1", {"start": v(19.8, -11.37) * mm, "end": v(26.8, -7.33) * mm});
            skLineSegment(sketch, "E74.2", {"start": v(26.8, -7.33) * mm, "end": v(33.8, -11.37) * mm});
            skLineSegment(sketch, "E74.3", {"start": v(33.8, -11.37) * mm, "end": v(33.8, -19.46) * mm});
            skLineSegment(sketch, "E74.4", {"start": v(33.8, -19.46) * mm, "end": v(26.8, -23.5) * mm});
            skLineSegment(sketch, "E74.5", {"start": v(26.8, -23.5) * mm, "end": v(19.8, -19.46) * mm});
            skPoint(sketch, "E74.0.midPoint", {"position": v(19.8, -15.42) * mm});
            skLineSegment(sketch, "E75", {"start": v(0.2, 0) * mm, "end": v(18.1, 0) * mm});
            skCircle(sketch, "E76.cCircle", {"center": v(18.1, 0) * mm, "radius": 7 * mm, "construction": true});
            skLineSegment(sketch, "E76.0", {"start": v(11.1, -4.04) * mm, "end": v(11.1, 4.04) * mm});
            skLineSegment(sketch, "E76.1", {"start": v(11.1, 4.04) * mm, "end": v(18.1, 8.08) * mm});
            skLineSegment(sketch, "E76.2", {"start": v(18.1, 8.08) * mm, "end": v(25.1, 4.04) * mm});
            skLineSegment(sketch, "E76.3", {"start": v(25.1, 4.04) * mm, "end": v(25.1, -4.04) * mm});
            skLineSegment(sketch, "E76.4", {"start": v(25.1, -4.04) * mm, "end": v(18.1, -8.08) * mm});
            skLineSegment(sketch, "E76.5", {"start": v(18.1, -8.08) * mm, "end": v(11.1, -4.04) * mm});
            skPoint(sketch, "E76.0.midPoint", {"position": v(11.1, 0) * mm});
            skLineSegment(sketch, "E77", {"start": v(18.1, 0) * mm, "end": v(36, 0) * mm});
            skCircle(sketch, "E78.cCircle", {"center": v(36, 0) * mm, "radius": 7 * mm, "construction": true});
            skLineSegment(sketch, "E78.0", {"start": v(29, -4.04) * mm, "end": v(29, 4.04) * mm});
            skLineSegment(sketch, "E78.1", {"start": v(29, 4.04) * mm, "end": v(36, 8.08) * mm});
            skLineSegment(sketch, "E78.2", {"start": v(36, 8.08) * mm, "end": v(43, 4.04) * mm});
            skLineSegment(sketch, "E78.3", {"start": v(43, 4.04) * mm, "end": v(43, -4.04) * mm});
            skLineSegment(sketch, "E78.4", {"start": v(43, -4.04) * mm, "end": v(36, -8.08) * mm});
            skLineSegment(sketch, "E78.5", {"start": v(36, -8.08) * mm, "end": v(29, -4.04) * mm});
            skPoint(sketch, "E78.0.midPoint", {"position": v(29, 0) * mm});
            skLineSegment(sketch, "E79", {"start": v(26.8, -15.42) * mm, "end": v(44.7, -15.42) * mm});
            skArc(sketch, "E80.cCircle", {"start": v(44.6, -8.42) * mm, "mid": v(37.7, -15.42) * mm, "end": v(44.6, -22.41) * mm, "construction": true});
            skLineSegment(sketch, "E80.0", {"start": v(37.7, -19.46) * mm, "end": v(37.7, -11.37) * mm});
            skLineSegment(sketch, "E80.1", {"start": v(37.7, -11.37) * mm, "end": v(44.7, -7.33) * mm});
            skLineSegment(sketch, "E80.5", {"start": v(44.7, -23.5) * mm, "end": v(37.7, -19.46) * mm});
            skPoint(sketch, "E80.0.midPoint", {"position": v(37.7, -15.42) * mm});
            skLineSegment(sketch, "E81", {"start": v(27.05, 15.5) * mm, "end": v(44.95, 15.5) * mm});
            skArc(sketch, "E82.cCircle", {"start": v(44.6, 22.5) * mm, "mid": v(37.95, 15.5) * mm, "end": v(44.6, 8.51) * mm, "construction": true});
            skLineSegment(sketch, "E82.0", {"start": v(37.95, 11.46) * mm, "end": v(37.95, 19.54) * mm});
            skLineSegment(sketch, "E82.1", {"start": v(37.95, 19.54) * mm, "end": v(44.95, 23.59) * mm});
            skLineSegment(sketch, "E82.5", {"start": v(44.95, 7.42) * mm, "end": v(37.95, 11.46) * mm});
            skPoint(sketch, "E82.0.midPoint", {"position": v(37.95, 15.5) * mm});
            skLineSegment(sketch, "E83", {"start": v(-26.65, 15.5) * mm, "end": v(-44.55, 15.5) * mm});
            skArc(sketch, "E84.cCircle", {"start": v(-44.6, 8.5) * mm, "mid": v(-37.55, 15.5) * mm, "end": v(-44.6, 22.5) * mm, "construction": true});
            skLineSegment(sketch, "E84.2", {"start": v(-44.55, 23.59) * mm, "end": v(-37.55, 19.54) * mm});
            skLineSegment(sketch, "E84.3", {"start": v(-37.55, 19.54) * mm, "end": v(-37.55, 11.46) * mm});
            skLineSegment(sketch, "E84.4", {"start": v(-37.55, 11.46) * mm, "end": v(-44.55, 7.42) * mm});
            skLineSegment(sketch, "E84.5", {"start": v(-44.55, 7.42) * mm, "end": v(-44.6, 7.45) * mm});
            skPoint(sketch, "E84.0.midPoint", {"position": v(-51.55, 15.5) * mm});
            skLineSegment(sketch, "E85", {"start": v(-26.7, -7.33) * mm, "end": v(-26.7, -23.5) * mm});
            skArc(sketch, "E86.cCircle", {"start": v(-44.6, -22.42) * mm, "mid": v(-37.6, -15.42) * mm, "end": v(-44.6, -8.42) * mm, "construction": true});
            skLineSegment(sketch, "E86.1", {"start": v(-44.6, -7.33) * mm, "end": v(-44.6, -7.33) * mm});
            skLineSegment(sketch, "E86.2", {"start": v(-44.6, -7.33) * mm, "end": v(-37.6, -11.37) * mm});
            skLineSegment(sketch, "E86.3", {"start": v(-37.6, -11.37) * mm, "end": v(-37.6, -19.46) * mm});
            skLineSegment(sketch, "E86.4", {"start": v(-37.6, -19.46) * mm, "end": v(-44.6, -23.5) * mm});
            skLineSegment(sketch, "E86.5", {"start": v(-44.6, -23.5) * mm, "end": v(-44.6, -23.5) * mm});
            skPoint(sketch, "E86.0.midPoint", {"position": v(-51.6, -15.42) * mm});
            skLineSegment(sketch, "E87", {"start": v(-8.75, 15.5) * mm, "end": v(0.2, 31) * mm});
            skArc(sketch, "E88.cCircle", {"start": v(-3.3, 24.94) * mm, "mid": v(0.2, 24) * mm, "end": v(3.7, 24.94) * mm, "construction": true});
            skLineSegment(sketch, "E88.4", {"start": v(3.7, 24.94) * mm, "end": v(0.2, 22.92) * mm});
            skLineSegment(sketch, "E88.5", {"start": v(0.2, 22.92) * mm, "end": v(-3.3, 24.94) * mm});
            skPoint(sketch, "E88.0.midPoint", {"position": v(-6.8, 31) * mm});
            skLineSegment(sketch, "E89.MirrorCS", {"start": v(0.2, -22.92) * mm, "end": v(-3.3, -24.94) * mm});
            skLineSegment(sketch, "E90.MirrorCS", {"start": v(3.7, -24.94) * mm, "end": v(0.2, -22.92) * mm});
            skLineSegment(sketch, "E91", {"start": v(0.2, 31) * mm, "end": v(-17.7, 31) * mm});
            skArc(sketch, "E92.cCircle", {"start": v(-21.2, 24.94) * mm, "mid": v(-17.7, 24) * mm, "end": v(-14.2, 24.94) * mm, "construction": true});
            skLineSegment(sketch, "E92.4", {"start": v(-14.2, 24.94) * mm, "end": v(-17.7, 22.92) * mm});
            skLineSegment(sketch, "E92.5", {"start": v(-17.7, 22.92) * mm, "end": v(-21.2, 24.94) * mm});
            skPoint(sketch, "E92.0.midPoint", {"position": v(-24.7, 31) * mm});
            skLineSegment(sketch, "E93", {"start": v(0.2, 31) * mm, "end": v(18.1, 31) * mm});
            skArc(sketch, "E94.cCircle", {"start": v(14.6, 24.94) * mm, "mid": v(18.1, 24) * mm, "end": v(21.6, 24.94) * mm, "construction": true});
            skLineSegment(sketch, "E94.4", {"start": v(21.6, 24.94) * mm, "end": v(18.1, 22.92) * mm});
            skLineSegment(sketch, "E94.5", {"start": v(18.1, 22.92) * mm, "end": v(14.6, 24.94) * mm});
            skPoint(sketch, "E94.0.midPoint", {"position": v(11.1, 31) * mm});
            skLineSegment(sketch, "E95", {"start": v(18.1, 31) * mm, "end": v(36, 31) * mm});
            skArc(sketch, "E96.cCircle", {"start": v(32.5, 24.94) * mm, "mid": v(36, 24) * mm, "end": v(39.5, 24.94) * mm, "construction": true});
            skLineSegment(sketch, "E96.4", {"start": v(39.5, 24.94) * mm, "end": v(36, 22.92) * mm});
            skLineSegment(sketch, "E96.5", {"start": v(36, 22.92) * mm, "end": v(32.5, 24.94) * mm});
            skPoint(sketch, "E96.0.midPoint", {"position": v(29, 31) * mm});
            skLineSegment(sketch, "E97", {"start": v(-17.7, 31) * mm, "end": v(-35.6, 31) * mm});
            skArc(sketch, "E98.cCircle", {"start": v(-39.1, 24.94) * mm, "mid": v(-35.6, 24) * mm, "end": v(-32.1, 24.94) * mm, "construction": true});
            skLineSegment(sketch, "E98.4", {"start": v(-32.1, 24.94) * mm, "end": v(-35.6, 22.92) * mm});
            skLineSegment(sketch, "E98.5", {"start": v(-35.6, 22.92) * mm, "end": v(-39.1, 24.94) * mm});
            skPoint(sketch, "E98.0.midPoint", {"position": v(-42.6, 31) * mm});
            skArc(sketch, "E99.MirrorC", {"start": v(32.5, -24.94) * mm, "mid": v(36, -24) * mm, "end": v(39.5, -24.94) * mm, "construction": true});
            skLineSegment(sketch, "E100.MirrorCS", {"start": v(39.5, -24.94) * mm, "end": v(36, -22.92) * mm});
            skLineSegment(sketch, "E101.MirrorCS", {"start": v(36, -22.92) * mm, "end": v(32.5, -24.94) * mm});
            skArc(sketch, "E102.MirrorC", {"start": v(14.6, -24.94) * mm, "mid": v(18.1, -24) * mm, "end": v(21.6, -24.94) * mm, "construction": true});
            skLineSegment(sketch, "E103.MirrorCS", {"start": v(21.6, -24.94) * mm, "end": v(18.1, -22.92) * mm});
            skLineSegment(sketch, "E104.MirrorCS", {"start": v(18.1, -22.92) * mm, "end": v(14.6, -24.94) * mm});
            skArc(sketch, "E105.MirrorC", {"start": v(-21.2, -24.94) * mm, "mid": v(-18.08, -24.02) * mm, "end": v(-14.87, -24.6) * mm, "construction": true});
            skLineSegment(sketch, "E106.MirrorCS", {"start": v(-14.8, -24.6) * mm, "end": v(-17.7, -22.92) * mm});
            skLineSegment(sketch, "E107.MirrorCS", {"start": v(-17.7, -22.92) * mm, "end": v(-21.2, -24.94) * mm});
            skLineSegment(sketch, "E108.MirrorCS", {"start": v(-32.1, -24.94) * mm, "end": v(-35.6, -22.92) * mm});
            skLineSegment(sketch, "E109.MirrorCS", {"start": v(-35.6, -22.92) * mm, "end": v(-39.1, -24.94) * mm});
            skLineSegment(sketch, "E110", {"start": v(44.6, 24.6) * mm, "end": v(-44.6, 24.6) * mm});
            skLineSegment(sketch, "E111", {"start": v(-44.6, 24.6) * mm, "end": v(-44.6, -24.6) * mm});
            skLineSegment(sketch, "E112", {"start": v(-44.6, -24.6) * mm, "end": v(44.6, -24.6) * mm});
            skLineSegment(sketch, "E113", {"start": v(44.6, -24.6) * mm, "end": v(44.6, 24.6) * mm});
            skPoint(sketch, "E114.orphan", {"position": v(29, 35.05) * mm});
            skPoint(sketch, "E115.orphan", {"position": v(29, 26.96) * mm});
            skPoint(sketch, "E116.orphan", {"position": v(25.1, 35.05) * mm});
            skPoint(sketch, "E94.0.end.orphan", {"position": v(11.1, 35.05) * mm});
            skPoint(sketch, "E117.orphan", {"position": v(11.1, 26.96) * mm});
            skPoint(sketch, "E118.orphan", {"position": v(7.2, 35.05) * mm});
            skPoint(sketch, "E119.orphan", {"position": v(-6.8, 35.05) * mm});
            skPoint(sketch, "E120.orphan", {"position": v(-6.8, 26.96) * mm});
            skPoint(sketch, "E121.orphan", {"position": v(-10.7, 26.96) * mm});
            skPoint(sketch, "E122.orphan", {"position": v(-24.7, 35.05) * mm});
            skPoint(sketch, "E123.orphan", {"position": v(-24.7, 26.96) * mm});
            skPoint(sketch, "E124.orphan", {"position": v(-42.6, 26.96) * mm});
            skPoint(sketch, "E98.1.start.orphan", {"position": v(-42.6, 35.05) * mm});
            skPoint(sketch, "E125.orphan", {"position": v(-28.6, 35.05) * mm});
            skLineSegment(sketch, "E126.trimOffspring", {"start": v(-44.6, 23.56) * mm, "end": v(-44.55, 23.59) * mm});
            skPoint(sketch, "E127.orphan", {"position": v(-51.55, 19.54) * mm});
            skPoint(sketch, "E128.orphan", {"position": v(-51.55, 11.46) * mm});
            skPoint(sketch, "E129.orphan", {"position": v(-51.6, -19.46) * mm});
            skPoint(sketch, "E86.0.end.orphan", {"position": v(-51.6, -11.37) * mm});
            skArc(sketch, "E130.trimOffspring", {"start": v(-39.1, -24.94) * mm, "mid": v(-35.6, -24) * mm, "end": v(-32.1, -24.94) * mm, "construction": true});
            skArc(sketch, "E131.trimOffspring", {"start": v(-3.3, -24.94) * mm, "mid": v(0.2, -24) * mm, "end": v(3.7, -24.94) * mm, "construction": true});
            skPoint(sketch, "E132.orphan", {"position": v(51.7, -11.37) * mm});
            skPoint(sketch, "E133.orphan", {"position": v(51.7, -19.46) * mm});
            skSolve(sketch);
        }
        {
            var Q0;
            {var subQ1=sQuery(id+"F6.wireOp",EDGE,"E71.1");Q0=makeQuery(id+"F6.imprint","IMPRINT",FACE,{"disambiguationData":[TD([[makeQuery(id+"F6.imprint","IMPRINT",EDGE,{"derivedFrom":subQ1}),-1.0]])]});}
            var Q1;
            {var subQ0=sQuery(id+"F6.wireOp",EDGE,"E71.4");Q1=makeQuery(id+"F6.imprint","IMPRINT",FACE,{"disambiguationData":[TD([[makeQuery(id+"F6.imprint","IMPRINT",EDGE,{"derivedFrom":subQ0}),-1.0]])]});}
            var Q2;
            {var subQ0=sQuery(id+"F6.wireOp",EDGE,"E113");var subQ1=sQuery(id+"F6.wireOp",EDGE,"E81");var subQ2=makeQuery(id+"F6.imprint","INTERSECT",VERTEX,{"derivedFrom":[subQ1,subQ0]});Q2=makeQuery(id+"F6.imprint","IMPRINT",FACE,{"disambiguationData":[TD([[makeQuery(id+"F6.imprint","IMPRINT",EDGE,{"disambiguationData":[TD([[subQ2,1.0]])],"derivedFrom":subQ1}),1.0]])]});}
            var Q3;
            {var subQ0=sQuery(id+"F6.wireOp",EDGE,"E113");var subQ1=sQuery(id+"F6.wireOp",EDGE,"E81");var subQ2=makeQuery(id+"F6.imprint","INTERSECT",VERTEX,{"derivedFrom":[subQ1,subQ0]});Q3=makeQuery(id+"F6.imprint","IMPRINT",FACE,{"disambiguationData":[TD([[makeQuery(id+"F6.imprint","IMPRINT",EDGE,{"disambiguationData":[TD([[subQ2,1.0]])],"derivedFrom":subQ1}),-1.0]])]});}
            var Q4;
            {var subQ0=sQuery(id+"F6.wireOp",EDGE,"E78.1");Q4=makeQuery(id+"F6.imprint","IMPRINT",FACE,{"disambiguationData":[TD([[makeQuery(id+"F6.imprint","IMPRINT",EDGE,{"derivedFrom":subQ0}),-1.0]])]});}
            var Q5;
            {var subQ0=sQuery(id+"F6.wireOp",EDGE,"E113");var subQ1=sQuery(id+"F6.wireOp",EDGE,"E79");var subQ2=makeQuery(id+"F6.imprint","INTERSECT",VERTEX,{"derivedFrom":[subQ1,subQ0]});Q5=makeQuery(id+"F6.imprint","IMPRINT",FACE,{"disambiguationData":[TD([[makeQuery(id+"F6.imprint","IMPRINT",EDGE,{"disambiguationData":[TD([[subQ2,1.0]])],"derivedFrom":subQ1}),1.0]])]});}
            var Q6;
            {var subQ0=sQuery(id+"F6.wireOp",EDGE,"E113");var subQ1=sQuery(id+"F6.wireOp",EDGE,"E79");var subQ2=makeQuery(id+"F6.imprint","INTERSECT",VERTEX,{"derivedFrom":[subQ1,subQ0]});Q6=makeQuery(id+"F6.imprint","IMPRINT",FACE,{"disambiguationData":[TD([[makeQuery(id+"F6.imprint","IMPRINT",EDGE,{"disambiguationData":[TD([[subQ2,1.0]])],"derivedFrom":subQ1}),-1.0]])]});}
            var Q7;
            {var subQ1=sQuery(id+"F6.wireOp",EDGE,"E74.1");Q7=makeQuery(id+"F6.imprint","IMPRINT",FACE,{"disambiguationData":[TD([[makeQuery(id+"F6.imprint","IMPRINT",EDGE,{"derivedFrom":subQ1}),-1.0]])]});}
            var Q8;
            {var subQ0=sQuery(id+"F6.wireOp",EDGE,"E74.4");Q8=makeQuery(id+"F6.imprint","IMPRINT",FACE,{"disambiguationData":[TD([[makeQuery(id+"F6.imprint","IMPRINT",EDGE,{"derivedFrom":subQ0}),-1.0]])]});}
            var Q9;
            {var subQ1=sQuery(id+"F6.wireOp",EDGE,"E76.1");Q9=makeQuery(id+"F6.imprint","IMPRINT",FACE,{"disambiguationData":[TD([[makeQuery(id+"F6.imprint","IMPRINT",EDGE,{"derivedFrom":subQ1}),-1.0]])]});}
            var Q10;
            {var subQ0=sQuery(id+"F6.wireOp",EDGE,"E76.4");Q10=makeQuery(id+"F6.imprint","IMPRINT",FACE,{"disambiguationData":[TD([[makeQuery(id+"F6.imprint","IMPRINT",EDGE,{"derivedFrom":subQ0}),-1.0]])]});}
            var Q11;
            {var subQ1=sQuery(id+"F6.wireOp",EDGE,"E69.1");Q11=makeQuery(id+"F6.imprint","IMPRINT",FACE,{"disambiguationData":[TD([[makeQuery(id+"F6.imprint","IMPRINT",EDGE,{"derivedFrom":subQ1}),-1.0]])]});}
            var Q12;
            {var subQ0=sQuery(id+"F6.wireOp",EDGE,"E69.4");Q12=makeQuery(id+"F6.imprint","IMPRINT",FACE,{"disambiguationData":[TD([[makeQuery(id+"F6.imprint","IMPRINT",EDGE,{"derivedFrom":subQ0}),-1.0]])]});}
            var Q13;
            {var subQ1=sQuery(id+"F6.wireOp",EDGE,"E65.1");Q13=makeQuery(id+"F6.imprint","IMPRINT",FACE,{"disambiguationData":[TD([[makeQuery(id+"F6.imprint","IMPRINT",EDGE,{"derivedFrom":subQ1}),-1.0]])]});}
            var Q14;
            {var subQ0=sQuery(id+"F6.wireOp",EDGE,"E65.3");var subQ1=sQuery(id+"F6.wireOp",EDGE,"E65.2");var subQ2=makeQuery(id+"F6.imprint","INTERSECT",VERTEX,{"derivedFrom":[subQ1,subQ0]});Q14=makeQuery(id+"F6.imprint","IMPRINT",FACE,{"disambiguationData":[TD([[makeQuery(id+"F6.imprint","IMPRINT",EDGE,{"disambiguationData":[TD([[subQ2,1.0]])],"derivedFrom":subQ1}),-1.0]])]});}
            var Q15;
            {var subQ0=sQuery(id+"F6.wireOp",EDGE,"E65.4");Q15=makeQuery(id+"F6.imprint","IMPRINT",FACE,{"disambiguationData":[TD([[makeQuery(id+"F6.imprint","IMPRINT",EDGE,{"derivedFrom":subQ0}),-1.0]])]});}
            var Q16;
            {var subQ1=sQuery(id+"F6.wireOp",EDGE,"E67.1");Q16=makeQuery(id+"F6.imprint","IMPRINT",FACE,{"disambiguationData":[TD([[makeQuery(id+"F6.imprint","IMPRINT",EDGE,{"derivedFrom":subQ1}),-1.0]])]});}
            var Q17;
            {var subQ0=sQuery(id+"F6.wireOp",EDGE,"E67.4");Q17=makeQuery(id+"F6.imprint","IMPRINT",FACE,{"disambiguationData":[TD([[makeQuery(id+"F6.imprint","IMPRINT",EDGE,{"derivedFrom":subQ0}),-1.0]])]});}
            var Q18;
            {var subQ1=sQuery(id+"F6.wireOp",EDGE,"E63.1");Q18=makeQuery(id+"F6.imprint","IMPRINT",FACE,{"disambiguationData":[TD([[makeQuery(id+"F6.imprint","IMPRINT",EDGE,{"derivedFrom":subQ1}),-1.0]])]});}
            var Q19;
            {var subQ0=sQuery(id+"F6.wireOp",EDGE,"E63.4");Q19=makeQuery(id+"F6.imprint","IMPRINT",FACE,{"disambiguationData":[TD([[makeQuery(id+"F6.imprint","IMPRINT",EDGE,{"derivedFrom":subQ0}),-1.0]])]});}
            var Q20;
            {var subQ6=sQuery(id+"F6.wireOp",EDGE,"E84.2");Q20=makeQuery(id+"F6.imprint","IMPRINT",FACE,{"disambiguationData":[TD([[makeQuery(id+"F6.imprint","IMPRINT",EDGE,{"derivedFrom":subQ6}),-1.0]])]});}
            var Q21;
            {var subQ0=sQuery(id+"F6.wireOp",EDGE,"E98.5");var subQ1=sQuery(id+"F6.wireOp",EDGE,"E98.4");var subQ2=makeQuery(id+"F6.imprint","INTERSECT",VERTEX,{"derivedFrom":[subQ1,subQ0]});Q21=makeQuery(id+"F6.imprint","IMPRINT",FACE,{"disambiguationData":[TD([[makeQuery(id+"F6.imprint","IMPRINT",EDGE,{"disambiguationData":[TD([[subQ2,1.0]])],"derivedFrom":subQ1}),-1.0]])]});}
            var Q22;
            {var subQ0=sQuery(id+"F6.wireOp",EDGE,"E92.5");var subQ1=sQuery(id+"F6.wireOp",EDGE,"E92.4");var subQ2=makeQuery(id+"F6.imprint","INTERSECT",VERTEX,{"derivedFrom":[subQ1,subQ0]});Q22=makeQuery(id+"F6.imprint","IMPRINT",FACE,{"disambiguationData":[TD([[makeQuery(id+"F6.imprint","IMPRINT",EDGE,{"disambiguationData":[TD([[subQ2,1.0]])],"derivedFrom":subQ1}),-1.0]])]});}
            var Q23;
            {var subQ0=sQuery(id+"F6.wireOp",EDGE,"E88.5");var subQ1=sQuery(id+"F6.wireOp",EDGE,"E88.4");var subQ2=makeQuery(id+"F6.imprint","INTERSECT",VERTEX,{"derivedFrom":[subQ1,subQ0]});Q23=makeQuery(id+"F6.imprint","IMPRINT",FACE,{"disambiguationData":[TD([[makeQuery(id+"F6.imprint","IMPRINT",EDGE,{"disambiguationData":[TD([[subQ2,1.0]])],"derivedFrom":subQ1}),-1.0]])]});}
            var Q24;
            {var subQ0=sQuery(id+"F6.wireOp",EDGE,"E94.5");var subQ1=sQuery(id+"F6.wireOp",EDGE,"E94.4");var subQ2=makeQuery(id+"F6.imprint","INTERSECT",VERTEX,{"derivedFrom":[subQ1,subQ0]});Q24=makeQuery(id+"F6.imprint","IMPRINT",FACE,{"disambiguationData":[TD([[makeQuery(id+"F6.imprint","IMPRINT",EDGE,{"disambiguationData":[TD([[subQ2,1.0]])],"derivedFrom":subQ1}),-1.0]])]});}
            var Q25;
            {var subQ0=sQuery(id+"F6.wireOp",EDGE,"E96.5");var subQ1=sQuery(id+"F6.wireOp",EDGE,"E96.4");var subQ2=makeQuery(id+"F6.imprint","INTERSECT",VERTEX,{"derivedFrom":[subQ1,subQ0]});Q25=makeQuery(id+"F6.imprint","IMPRINT",FACE,{"disambiguationData":[TD([[makeQuery(id+"F6.imprint","IMPRINT",EDGE,{"disambiguationData":[TD([[subQ2,1.0]])],"derivedFrom":subQ1}),-1.0]])]});}
            var Q26;
            {var subQ0=sQuery(id+"F6.wireOp",EDGE,"E101.MirrorCS");var subQ1=sQuery(id+"F6.wireOp",EDGE,"E100.MirrorCS");var subQ2=makeQuery(id+"F6.imprint","INTERSECT",VERTEX,{"derivedFrom":[subQ1,subQ0]});Q26=makeQuery(id+"F6.imprint","IMPRINT",FACE,{"disambiguationData":[TD([[makeQuery(id+"F6.imprint","IMPRINT",EDGE,{"disambiguationData":[TD([[subQ2,1.0]])],"derivedFrom":subQ1}),1.0]])]});}
            var Q27;
            {var subQ0=sQuery(id+"F6.wireOp",EDGE,"E104.MirrorCS");var subQ1=sQuery(id+"F6.wireOp",EDGE,"E103.MirrorCS");var subQ2=makeQuery(id+"F6.imprint","INTERSECT",VERTEX,{"derivedFrom":[subQ1,subQ0]});Q27=makeQuery(id+"F6.imprint","IMPRINT",FACE,{"disambiguationData":[TD([[makeQuery(id+"F6.imprint","IMPRINT",EDGE,{"disambiguationData":[TD([[subQ2,1.0]])],"derivedFrom":subQ1}),1.0]])]});}
            var Q28;
            {var subQ0=sQuery(id+"F6.wireOp",EDGE,"E90.MirrorCS");var subQ1=sQuery(id+"F6.wireOp",EDGE,"E89.MirrorCS");var subQ2=makeQuery(id+"F6.imprint","INTERSECT",VERTEX,{"derivedFrom":[subQ1,subQ0]});Q28=makeQuery(id+"F6.imprint","IMPRINT",FACE,{"disambiguationData":[TD([[makeQuery(id+"F6.imprint","IMPRINT",EDGE,{"disambiguationData":[TD([[subQ2,-1.0]])],"derivedFrom":subQ1}),1.0]])]});}
            var Q29;
            {var subQ0=sQuery(id+"F6.wireOp",EDGE,"E106.MirrorCS");Q29=makeQuery(id+"F6.imprint","IMPRINT",FACE,{"disambiguationData":[TD([[makeQuery(id+"F6.imprint","IMPRINT",EDGE,{"derivedFrom":subQ0}),1.0]])]});}
            var Q30;
            {var subQ0=sQuery(id+"F6.wireOp",EDGE,"E109.MirrorCS");var subQ1=sQuery(id+"F6.wireOp",EDGE,"E108.MirrorCS");var subQ2=makeQuery(id+"F6.imprint","INTERSECT",VERTEX,{"derivedFrom":[subQ1,subQ0]});Q30=makeQuery(id+"F6.imprint","IMPRINT",FACE,{"disambiguationData":[TD([[makeQuery(id+"F6.imprint","IMPRINT",EDGE,{"disambiguationData":[TD([[subQ2,1.0]])],"derivedFrom":subQ1}),1.0]])]});}
            extrude(context, id + "F7", {"entities" : qUnion([Q0, Q1, Q2, Q3, Q4, Q5, Q6, Q7, Q8, Q9, Q10, Q11, Q12, Q13, Q14, Q15, Q16, Q17, Q18, Q19, Q20, Q21, Q22, Q23, Q24, Q25, Q26, Q27, Q28, Q29, Q30]), "operationType" : NewBodyOperationType.REMOVE, "oppositeDirection" : true, "depth" : 25 * mm});
        }
        {
            var Q0;
            Q0=makeQuery(id+"F1.opExtrude","CAP_FACE",FACE,{"disambiguationData":[OSD([sQuery(id+"F0.wireOp",EDGE,"E0.bottom"),sQuery(id+"F0.wireOp",EDGE,"E0.top"),sQuery(id+"F0.wireOp",EDGE,"E0.left"),sQuery(id+"F0.wireOp",EDGE,"E0.right")])],"isStart":false});
            var sketch = newSketch(context, id + "F8", { "sketchPlane" : qUnion([Q0])});
            skCircle(sketch, "E134.cCircle", {"center": v(-44.6, -15.42) * mm, "radius": 6.95 * mm, "construction": true});
            skPoint(sketch, "E134.cCircle.centerSnap0", {"position": v(-33.7, -15.42) * mm});
            skLineSegment(sketch, "E134.0", {"start": v(-51.55, -19.43) * mm, "end": v(-51.55, -11.4) * mm});
            skLineSegment(sketch, "E134.1", {"start": v(-51.55, -11.4) * mm, "end": v(-44.6, -7.4) * mm});
            skLineSegment(sketch, "E134.2", {"start": v(-44.6, -7.4) * mm, "end": v(-37.65, -11.4) * mm});
            skLineSegment(sketch, "E134.3", {"start": v(-37.65, -11.4) * mm, "end": v(-37.65, -19.43) * mm});
            skLineSegment(sketch, "E134.4", {"start": v(-37.65, -19.43) * mm, "end": v(-44.6, -23.44) * mm});
            skLineSegment(sketch, "E134.5", {"start": v(-44.6, -23.44) * mm, "end": v(-51.55, -19.43) * mm});
            skPoint(sketch, "E134.0.midPoint", {"position": v(-51.55, -15.42) * mm});
            skLineSegment(sketch, "E135", {"start": v(-44.6, -7.4) * mm, "end": v(-44.6, -23.44) * mm});
            skSolve(sketch);
        }
        {
            var Q0;
            Q0=makeQuery(id+"F8.imprint","IMPRINT",FACE,{"disambiguationData":[TD([[makeQuery(id+"F8.imprint","IMPRINT",EDGE,{"derivedFrom":sQuery(id+"F8.wireOp",EDGE,"E134.2")}),-1.0]])]});
            extrude(context, id + "F9", {"entities" : qUnion([Q0]), "operationType" : NewBodyOperationType.REMOVE, "oppositeDirection" : true, "depth" : 25 * mm});
        }
    });
